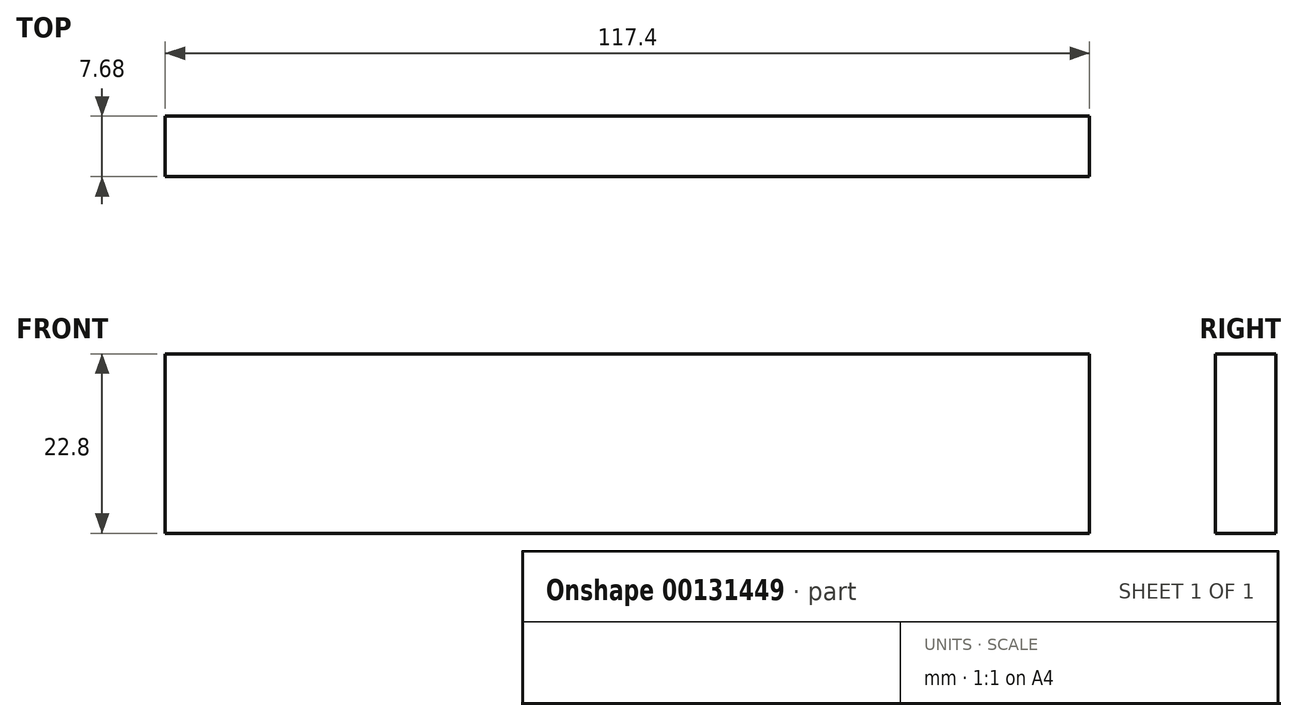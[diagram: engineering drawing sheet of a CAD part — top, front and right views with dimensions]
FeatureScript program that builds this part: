
annotation { "Feature Type Name" : "Feature", "Feature Type Description" : "" }
export const myFeature = defineFeature(function(context is Context, id is Id, definition is map)
    precondition{}
    {
        {
            var Q0;
            Q0=qCreatedBy(makeId("Front.planeOp"),FACE);
            var sketch = newSketch(context, id + "F0", { "sketchPlane" : qUnion([Q0])});
            skLineSegment(sketch, "E0.bottom", {"start": v(-54, 10.82) * mm, "end": v(63.4, 10.82) * mm});
            skLineSegment(sketch, "E0.top", {"start": v(-54, -11.98) * mm, "end": v(63.4, -11.98) * mm});
            skLineSegment(sketch, "E0.left", {"start": v(-54, 10.82) * mm, "end": v(-54, -11.98) * mm});
            skLineSegment(sketch, "E0.right", {"start": v(63.4, 10.82) * mm, "end": v(63.4, -11.98) * mm});
            skSolve(sketch);
        }
        {
            var Q0;
            Q0 = qSketchRegion(id + "F0", true);
            extrude(context, id + "F1", {"entities" : qUnion([Q0]), "depth" : 7.68 * mm});
        }
    });
